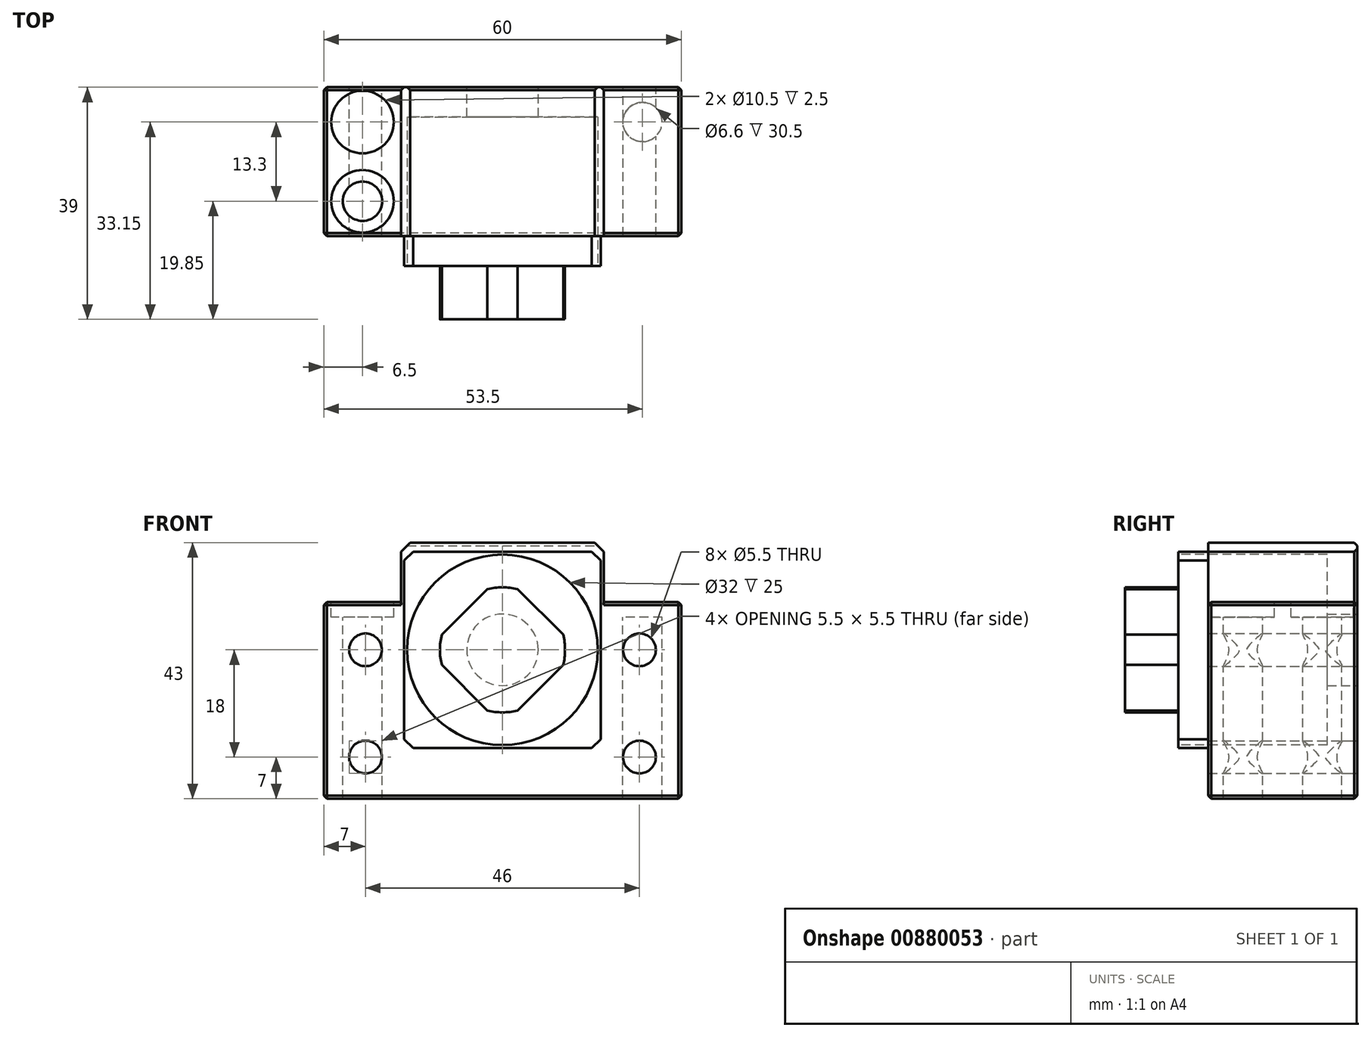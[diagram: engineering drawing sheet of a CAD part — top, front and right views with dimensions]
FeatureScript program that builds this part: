
annotation { "Feature Type Name" : "Feature", "Feature Type Description" : "" }
export const myFeature = defineFeature(function(context is Context, id is Id, definition is map)
    precondition{}
    {
        {
            var Q0;
            Q0=qCreatedBy(makeId("Front.planeOp"),FACE);
            var sketch = newSketch(context, id + "F0", { "sketchPlane" : qUnion([Q0])});
            skLineSegment(sketch, "E0", {"start": v(0, 18) * mm, "end": v(17, 18) * mm});
            skLineSegment(sketch, "E1", {"start": v(17, 18) * mm, "end": v(17, 8) * mm});
            skLineSegment(sketch, "E2", {"start": v(17, 8) * mm, "end": v(30, 8) * mm});
            skLineSegment(sketch, "E3", {"start": v(30, 8) * mm, "end": v(30, -25) * mm});
            skLineSegment(sketch, "E4", {"start": v(30, -25) * mm, "end": v(0, -25) * mm});
            skLineSegment(sketch, "E5.MirrorCS", {"start": v(0, 18) * mm, "end": v(-17, 18) * mm});
            skLineSegment(sketch, "E6.MirrorCS", {"start": v(-17, 8) * mm, "end": v(-30, 8) * mm});
            skLineSegment(sketch, "E7.MirrorCS", {"start": v(-30, -25) * mm, "end": v(0, -25) * mm});
            skLineSegment(sketch, "E8.MirrorCS", {"start": v(-17, 18) * mm, "end": v(-17, 8) * mm});
            skLineSegment(sketch, "E9.MirrorCS", {"start": v(-30, 8) * mm, "end": v(-30, -25) * mm});
            skCircle(sketch, "E10", {"center": v(0, 0) * mm, "radius": 6 * mm});
            skCircle(sketch, "E11", {"center": v(23, 0) * mm, "radius": 2.75 * mm});
            skCircle(sketch, "E12", {"center": v(23, -18) * mm, "radius": 2.75 * mm});
            skCircle(sketch, "E13.MirrorC", {"center": v(-23, -18) * mm, "radius": 2.75 * mm});
            skCircle(sketch, "E14.MirrorC", {"center": v(-23, 0) * mm, "radius": 2.75 * mm});
            skSolve(sketch);
        }
        {
            var Q0;
            Q0=makeQuery(id+"F0.imprint","IMPRINT",FACE,{"disambiguationData":[TD([[makeQuery(id+"F0.imprint","IMPRINT",EDGE,{"derivedFrom":sQuery(id+"F0.wireOp",EDGE,"E0")}),-1.0]])]});
            extrude(context, id + "F1", {"entities" : qUnion([Q0]), "endBound" : BoundingType.SYMMETRIC, "depth" : 25 * mm});
        }
        {
            var Q0;
            Q0=makeQuery(id+"F1.opExtrude","SWEPT_EDGE",EDGE,{"disambiguationData":[OSD([sQuery(id+"F0.wireOp",EDGE,"E0"),sQuery(id+"F0.wireOp",EDGE,"E1")])]});
            var Q1;
            Q1=makeQuery(id+"F1.opExtrude","SWEPT_EDGE",EDGE,{"disambiguationData":[OSD([sQuery(id+"F0.wireOp",EDGE,"E5.MirrorCS"),sQuery(id+"F0.wireOp",EDGE,"E8.MirrorCS")])]});
            chamfer(context, id + "F2", {"entities" : qUnion([Q0, Q1]), "width" : 1.5 * mm, "tangentPropagation" : true});
        }
        {
            var Q0;
            Q0=makeQuery(id+"F1.opExtrude","CAP_FACE",FACE,{"disambiguationData":[OSD([sQuery(id+"F0.wireOp",EDGE,"E0"),sQuery(id+"F0.wireOp",EDGE,"E1"),sQuery(id+"F0.wireOp",EDGE,"E2"),sQuery(id+"F0.wireOp",EDGE,"E3"),sQuery(id+"F0.wireOp",EDGE,"E4"),sQuery(id+"F0.wireOp",EDGE,"E5.MirrorCS"),sQuery(id+"F0.wireOp",EDGE,"E6.MirrorCS"),sQuery(id+"F0.wireOp",EDGE,"E7.MirrorCS"),sQuery(id+"F0.wireOp",EDGE,"E8.MirrorCS"),sQuery(id+"F0.wireOp",EDGE,"E9.MirrorCS"),sQuery(id+"F0.wireOp",EDGE,"E10")])],"isStart":false});
            var sketch = newSketch(context, id + "F3", { "sketchPlane" : qUnion([Q0])});
            skCircle(sketch, "E15", {"center": v(0, 0) * mm, "radius": 16 * mm});
            skSolve(sketch);
        }
        {
            var Q0;
            Q0=makeQuery(id+"F3.imprint","IMPRINT",FACE,{"disambiguationData":[TD([[makeQuery(id+"F3.imprint","IMPRINT",EDGE,{"derivedFrom":sQuery(id+"F3.wireOp",EDGE,"E15")}),1.0]])]});
            extrude(context, id + "F4", {"entities" : qUnion([Q0]), "operationType" : NewBodyOperationType.REMOVE, "oppositeDirection" : true, "depth" : 20 * mm});
        }
        {
            var Q0;
            Q0=makeQuery(id+"F1.opExtrude","CAP_FACE",FACE,{"disambiguationData":[OSD([sQuery(id+"F0.wireOp",EDGE,"E0"),sQuery(id+"F0.wireOp",EDGE,"E1"),sQuery(id+"F0.wireOp",EDGE,"E2"),sQuery(id+"F0.wireOp",EDGE,"E3"),sQuery(id+"F0.wireOp",EDGE,"E4"),sQuery(id+"F0.wireOp",EDGE,"E5.MirrorCS"),sQuery(id+"F0.wireOp",EDGE,"E6.MirrorCS"),sQuery(id+"F0.wireOp",EDGE,"E7.MirrorCS"),sQuery(id+"F0.wireOp",EDGE,"E8.MirrorCS"),sQuery(id+"F0.wireOp",EDGE,"E9.MirrorCS"),sQuery(id+"F0.wireOp",EDGE,"E10")])],"isStart":false});
            var sketch = newSketch(context, id + "F5", { "sketchPlane" : qUnion([Q0])});
            skLineSegment(sketch, "E16.bottom", {"start": v(-16.5, 16.5) * mm, "end": v(16.5, 16.5) * mm});
            skLineSegment(sketch, "E16.top", {"start": v(-16.5, -16.5) * mm, "end": v(16.5, -16.5) * mm});
            skLineSegment(sketch, "E16.left", {"start": v(-16.5, 16.5) * mm, "end": v(-16.5, -16.5) * mm});
            skLineSegment(sketch, "E16.right", {"start": v(16.5, 16.5) * mm, "end": v(16.5, -16.5) * mm});
            skCircle(sketch, "E17", {"center": v(0, 0) * mm, "radius": 6 * mm});
            skSolve(sketch);
        }
        {
            var Q0;
            Q0=makeQuery(id+"F5.imprint","IMPRINT",FACE,{"disambiguationData":[TD([[makeQuery(id+"F5.imprint","IMPRINT",EDGE,{"derivedFrom":sQuery(id+"F5.wireOp",EDGE,"E16.bottom")}),-1.0]])]});
            var Q1;
            Q1=makeQuery(id+"F5.imprint","IMPRINT",FACE,{"disambiguationData":[TD([[makeQuery(id+"F5.imprint","IMPRINT",EDGE,{"derivedFrom":makeQuery(id+"F4.boolean.opBoolean","COPY",EDGE,{"derivedFrom":makeQuery(id+"F4.opExtrude","CAP_EDGE",EDGE,{"disambiguationData":[OSD([sQuery(id+"F3.wireOp",EDGE,"E15")])],"isStart":true})})}),1.0]])]});
            extrude(context, id + "F6", {"entities" : qUnion([Q0, Q1]), "operationType" : NewBodyOperationType.ADD, "depth" : 5 * mm, "hasSecondDirection" : true, "secondDirectionOppositeDirection" : true, "secondDirectionDepth" : 2 * mm});
        }
        {
            var Q0;
            Q0=makeQuery(id+"F6.opExtrude","SWEPT_EDGE",EDGE,{"disambiguationData":[OSD([sQuery(id+"F0.wireOp",EDGE,"E0"),sQuery(id+"F0.wireOp",EDGE,"E1"),sQuery(id+"F0.wireOp",EDGE,"E2"),sQuery(id+"F0.wireOp",EDGE,"E3"),sQuery(id+"F0.wireOp",EDGE,"E4"),sQuery(id+"F0.wireOp",EDGE,"E5.MirrorCS"),sQuery(id+"F0.wireOp",EDGE,"E6.MirrorCS"),sQuery(id+"F0.wireOp",EDGE,"E7.MirrorCS"),sQuery(id+"F0.wireOp",EDGE,"E8.MirrorCS"),sQuery(id+"F0.wireOp",EDGE,"E9.MirrorCS"),sQuery(id+"F0.wireOp",EDGE,"E10"),sQuery(id+"F5.wireOp",EDGE,"E16.bottom"),sQuery(id+"F5.wireOp",EDGE,"E16.left")])]});
            var Q1;
            Q1=makeQuery(id+"F6.opExtrude","SWEPT_EDGE",EDGE,{"disambiguationData":[OSD([sQuery(id+"F0.wireOp",EDGE,"E0"),sQuery(id+"F0.wireOp",EDGE,"E1"),sQuery(id+"F0.wireOp",EDGE,"E2"),sQuery(id+"F0.wireOp",EDGE,"E3"),sQuery(id+"F0.wireOp",EDGE,"E4"),sQuery(id+"F0.wireOp",EDGE,"E5.MirrorCS"),sQuery(id+"F0.wireOp",EDGE,"E6.MirrorCS"),sQuery(id+"F0.wireOp",EDGE,"E7.MirrorCS"),sQuery(id+"F0.wireOp",EDGE,"E8.MirrorCS"),sQuery(id+"F0.wireOp",EDGE,"E9.MirrorCS"),sQuery(id+"F0.wireOp",EDGE,"E10"),sQuery(id+"F5.wireOp",EDGE,"E16.bottom"),sQuery(id+"F5.wireOp",EDGE,"E16.right")])]});
            var Q2;
            Q2=makeQuery(id+"F6.opExtrude","SWEPT_EDGE",EDGE,{"disambiguationData":[OSD([sQuery(id+"F5.wireOp",EDGE,"E16.top"),sQuery(id+"F5.wireOp",EDGE,"E16.right")])]});
            var Q3;
            Q3=makeQuery(id+"F6.opExtrude","SWEPT_EDGE",EDGE,{"disambiguationData":[OSD([sQuery(id+"F5.wireOp",EDGE,"E16.top"),sQuery(id+"F5.wireOp",EDGE,"E16.left")])]});
            chamfer(context, id + "F7", {"entities" : qUnion([Q0, Q1, Q2, Q3]), "width" : 1.5 * mm, "tangentPropagation" : true});
        }
        {
            var Q0;
            Q0=makeQuery(id+"F1.opExtrude","SWEPT_FACE",FACE,{"disambiguationData":[OSD([sQuery(id+"F0.wireOp",EDGE,"E6.MirrorCS")])]});
            var sketch = newSketch(context, id + "F8", { "sketchPlane" : qUnion([Q0])});
            skCircle(sketch, "E18", {"center": v(-23.5, -6.65) * mm, "radius": 5.25 * mm});
            skPoint(sketch, "E18.centerSnap0", {"position": v(-23.5, -12.5) * mm});
            skCircle(sketch, "E19", {"center": v(-23.5, 6.65) * mm, "radius": 5.25 * mm});
            skPoint(sketch, "E19.centerSnap0", {"position": v(-23.5, 12.5) * mm});
            skCircle(sketch, "E20.MirrorC", {"center": v(23.5, 6.65) * mm, "radius": 5.25 * mm});
            skCircle(sketch, "E21.MirrorC", {"center": v(23.5, -6.65) * mm, "radius": 5.25 * mm});
            skSolve(sketch);
        }
        {
            var Q0;
            Q0=makeQuery(id+"F8.imprint","IMPRINT",FACE,{"disambiguationData":[TD([[makeQuery(id+"F8.imprint","IMPRINT",EDGE,{"derivedFrom":sQuery(id+"F8.wireOp",EDGE,"E20.MirrorC")}),-1.0]])]});
            var Q1;
            Q1=makeQuery(id+"F8.imprint","IMPRINT",FACE,{"disambiguationData":[TD([[makeQuery(id+"F8.imprint","IMPRINT",EDGE,{"derivedFrom":sQuery(id+"F8.wireOp",EDGE,"E21.MirrorC")}),-1.0]])]});
            var Q2;
            Q2=makeQuery(id+"F8.imprint","IMPRINT",FACE,{"disambiguationData":[TD([[makeQuery(id+"F8.imprint","IMPRINT",EDGE,{"derivedFrom":sQuery(id+"F8.wireOp",EDGE,"E18")}),1.0]])]});
            var Q3;
            Q3=makeQuery(id+"F8.imprint","IMPRINT",FACE,{"disambiguationData":[TD([[makeQuery(id+"F8.imprint","IMPRINT",EDGE,{"derivedFrom":sQuery(id+"F8.wireOp",EDGE,"E19")}),1.0]])]});
            extrude(context, id + "F9", {"entities" : qUnion([Q0, Q1, Q2, Q3]), "operationType" : NewBodyOperationType.REMOVE, "oppositeDirection" : true, "depth" : 2.5 * mm});
        }
        {
            var Q0;
            Q0=makeQuery(id+"F9.boolean.opBoolean","COPY",FACE,{"derivedFrom":makeQuery(id+"F9.opExtrude","CAP_FACE",FACE,{"disambiguationData":[OSD([sQuery(id+"F8.wireOp",EDGE,"E18")])],"isStart":false})});
            var sketch = newSketch(context, id + "F10", { "sketchPlane" : qUnion([Q0])});
            skCircle(sketch, "E22", {"center": v(-23.5, -6.65) * mm, "radius": 3.3 * mm});
            skCircle(sketch, "E23.MirrorC", {"center": v(-23.5, 6.65) * mm, "radius": 3.3 * mm});
            skCircle(sketch, "E24.MirrorC", {"center": v(23.5, 6.65) * mm, "radius": 3.3 * mm});
            skCircle(sketch, "E25.MirrorC", {"center": v(23.5, -6.65) * mm, "radius": 3.3 * mm});
            skSolve(sketch);
        }
        {
            var Q0;
            Q0=makeQuery(id+"F10.imprint","IMPRINT",FACE,{"disambiguationData":[TD([[makeQuery(id+"F10.imprint","IMPRINT",EDGE,{"derivedFrom":sQuery(id+"F10.wireOp",EDGE,"E22")}),1.0]])]});
            var Q1;
            Q1=makeQuery(id+"F10.imprint","IMPRINT",FACE,{"disambiguationData":[TD([[makeQuery(id+"F10.imprint","IMPRINT",EDGE,{"derivedFrom":sQuery(id+"F10.wireOp",EDGE,"E23.MirrorC")}),-1.0]])]});
            var Q2;
            Q2=makeQuery(id+"F10.imprint","IMPRINT",FACE,{"disambiguationData":[TD([[makeQuery(id+"F10.imprint","IMPRINT",EDGE,{"derivedFrom":sQuery(id+"F10.wireOp",EDGE,"E24.MirrorC")}),1.0]])]});
            var Q3;
            Q3=makeQuery(id+"F10.imprint","IMPRINT",FACE,{"disambiguationData":[TD([[makeQuery(id+"F10.imprint","IMPRINT",EDGE,{"derivedFrom":sQuery(id+"F10.wireOp",EDGE,"E25.MirrorC")}),-1.0]])]});
            var Q4;
            Q4=makeQuery(id+"F1.opExtrude","SWEPT_FACE",FACE,{"disambiguationData":[OSD([sQuery(id+"F0.wireOp",EDGE,"E4"),sQuery(id+"F0.wireOp",EDGE,"E7.MirrorCS")])]});
            extrude(context, id + "F11", {"entities" : qUnion([Q0, Q1, Q2, Q3]), "operationType" : NewBodyOperationType.REMOVE, "endBound" : BoundingType.UP_TO_SURFACE, "oppositeDirection" : true, "endBoundEntityFace" : qUnion([Q4]), "depth" : 25 * mm});
        }
        {
            var Q0;
            Q0=makeQuery(id+"F6.opExtrude","CAP_FACE",FACE,{"disambiguationData":[OSD([sQuery(id+"F5.wireOp",EDGE,"E16.bottom"),sQuery(id+"F5.wireOp",EDGE,"E16.top"),sQuery(id+"F5.wireOp",EDGE,"E16.left"),sQuery(id+"F5.wireOp",EDGE,"E16.right"),sQuery(id+"F5.wireOp",EDGE,"E17")])],"isStart":false});
            var sketch = newSketch(context, id + "F12", { "sketchPlane" : qUnion([Q0])});
            skArc(sketch, "E26", {"start": v(-10.19, 2.54) * mm, "mid": v(-10.5, 0) * mm, "end": v(-10.19, -2.54) * mm});
            skLineSegment(sketch, "E27", {"start": v(-10.19, 2.54) * mm, "end": v(-2.54, 10.19) * mm});
            skLineSegment(sketch, "E28", {"start": v(2.54, 10.19) * mm, "end": v(10.19, 2.54) * mm});
            skLineSegment(sketch, "E29", {"start": v(10.19, -2.54) * mm, "end": v(2.54, -10.19) * mm});
            skLineSegment(sketch, "E30", {"start": v(-2.54, -10.19) * mm, "end": v(-10.19, -2.54) * mm});
            skPoint(sketch, "E31.orphan", {"position": v(0, 12.73) * mm});
            skArc(sketch, "E32.trimOffspring", {"start": v(2.54, 10.19) * mm, "mid": v(0, 10.5) * mm, "end": v(-2.54, 10.19) * mm});
            skPoint(sketch, "E33.orphan", {"position": v(12.73, 0) * mm});
            skArc(sketch, "E34.trimOffspring", {"start": v(10.19, -2.54) * mm, "mid": v(10.5, 0) * mm, "end": v(10.19, 2.54) * mm});
            skPoint(sketch, "E35.orphan", {"position": v(0, -12.73) * mm});
            skArc(sketch, "E36.trimOffspring", {"start": v(-2.54, -10.19) * mm, "mid": v(0, -10.5) * mm, "end": v(2.54, -10.19) * mm});
            skPoint(sketch, "E37.orphan", {"position": v(-12.73, 0) * mm});
            skSolve(sketch);
        }
        {
            var Q0;
            Q0=makeQuery(id+"F12.imprint","IMPRINT",FACE,{"disambiguationData":[TD([[makeQuery(id+"F12.imprint","IMPRINT",EDGE,{"derivedFrom":sQuery(id+"F12.wireOp",EDGE,"E26")}),1.0]])]});
            extrude(context, id + "F13", {"entities" : qUnion([Q0]), "operationType" : NewBodyOperationType.ADD, "depth" : 9 * mm});
        }
        {
            var Q0;
            Q0=makeQuery(id+"F1.opExtrude","SWEPT_EDGE",EDGE,{"disambiguationData":[OSD([sQuery(id+"F0.wireOp",EDGE,"E2"),sQuery(id+"F0.wireOp",EDGE,"E3")])]});
            var Q1;
            Q1=makeQuery(id+"F1.opExtrude","SWEPT_EDGE",EDGE,{"disambiguationData":[OSD([sQuery(id+"F0.wireOp",EDGE,"E3"),sQuery(id+"F0.wireOp",EDGE,"E4")])]});
            var Q2;
            Q2=makeQuery(id+"F1.opExtrude","SWEPT_EDGE",EDGE,{"disambiguationData":[OSD([sQuery(id+"F0.wireOp",EDGE,"E6.MirrorCS"),sQuery(id+"F0.wireOp",EDGE,"E9.MirrorCS")])]});
            var Q3;
            Q3=makeQuery(id+"F1.opExtrude","SWEPT_EDGE",EDGE,{"disambiguationData":[OSD([sQuery(id+"F0.wireOp",EDGE,"E7.MirrorCS"),sQuery(id+"F0.wireOp",EDGE,"E9.MirrorCS")])]});
            var Q4;
            Q4=makeQuery(id+"F1.opExtrude","CAP_EDGE",EDGE,{"disambiguationData":[OSD([sQuery(id+"F0.wireOp",EDGE,"E9.MirrorCS")])],"isStart":false});
            var Q5;
            Q5=makeQuery(id+"F1.opExtrude","CAP_EDGE",EDGE,{"disambiguationData":[OSD([sQuery(id+"F0.wireOp",EDGE,"E4"),sQuery(id+"F0.wireOp",EDGE,"E7.MirrorCS")])],"isStart":false});
            var Q6;
            Q6=makeQuery(id+"F1.opExtrude","CAP_EDGE",EDGE,{"disambiguationData":[OSD([sQuery(id+"F0.wireOp",EDGE,"E3")])],"isStart":false});
            var Q7;
            Q7=makeQuery(id+"F1.opExtrude","CAP_EDGE",EDGE,{"disambiguationData":[OSD([sQuery(id+"F0.wireOp",EDGE,"E4"),sQuery(id+"F0.wireOp",EDGE,"E7.MirrorCS")])],"isStart":true});
            var Q8;
            Q8=makeQuery(id+"F1.opExtrude","CAP_EDGE",EDGE,{"disambiguationData":[OSD([sQuery(id+"F0.wireOp",EDGE,"E3")])],"isStart":true});
            var Q9;
            Q9=makeQuery(id+"F1.opExtrude","CAP_EDGE",EDGE,{"disambiguationData":[OSD([sQuery(id+"F0.wireOp",EDGE,"E2")])],"isStart":true});
            var Q10;
            Q10=makeQuery(id+"F1.opExtrude","CAP_EDGE",EDGE,{"disambiguationData":[OSD([sQuery(id+"F0.wireOp",EDGE,"E1")])],"isStart":true});
            var Q11;
            Q11=makeQuery(id+"F1.opExtrude","CAP_EDGE",EDGE,{"disambiguationData":[OSD([sQuery(id+"F0.wireOp",EDGE,"E0"),sQuery(id+"F0.wireOp",EDGE,"E5.MirrorCS")])],"isStart":true});
            var Q12;
            Q12=makeQuery(id+"F1.opExtrude","CAP_EDGE",EDGE,{"disambiguationData":[OSD([sQuery(id+"F0.wireOp",EDGE,"E8.MirrorCS")])],"isStart":true});
            var Q13;
            Q13=makeQuery(id+"F1.opExtrude","CAP_EDGE",EDGE,{"disambiguationData":[OSD([sQuery(id+"F0.wireOp",EDGE,"E6.MirrorCS")])],"isStart":true});
            var Q14;
            Q14=makeQuery(id+"F1.opExtrude","CAP_EDGE",EDGE,{"disambiguationData":[OSD([sQuery(id+"F0.wireOp",EDGE,"E9.MirrorCS")])],"isStart":true});
            var Q15;
            Q15=makeQuery(id+"F1.opExtrude","CAP_EDGE",EDGE,{"disambiguationData":[OSD([sQuery(id+"F0.wireOp",EDGE,"E6.MirrorCS")])],"isStart":false});
            var Q16;
            Q16=makeQuery(id+"F1.opExtrude","CAP_EDGE",EDGE,{"disambiguationData":[OSD([sQuery(id+"F0.wireOp",EDGE,"E2")])],"isStart":false});
            chamfer(context, id + "F14", {"entities" : qUnion([Q0, Q1, Q2, Q3, Q4, Q5, Q6, Q7, Q8, Q9, Q10, Q11, Q12, Q13, Q14, Q15, Q16]), "width" : 0.5 * mm, "tangentPropagation" : true});
        }
    });
